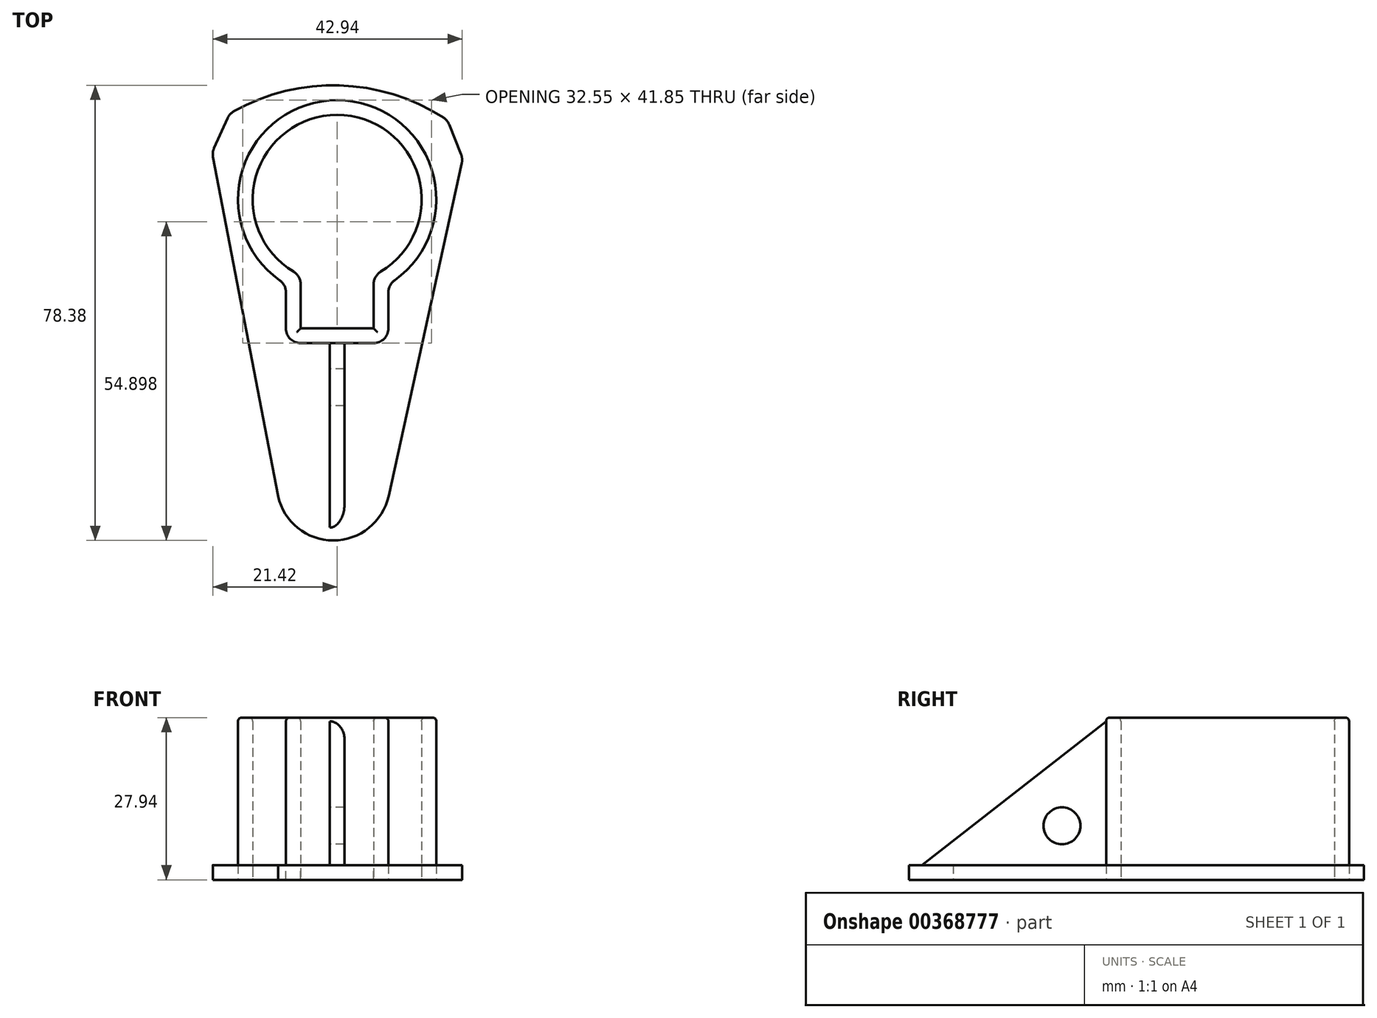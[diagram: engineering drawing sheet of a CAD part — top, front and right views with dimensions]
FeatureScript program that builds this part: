
annotation { "Feature Type Name" : "Feature", "Feature Type Description" : "" }
export const myFeature = defineFeature(function(context is Context, id is Id, definition is map)
    precondition{}
    {
        {
            var Q0;
            Q0=qCreatedBy(makeId("Top.planeOp"),FACE);
            var sketch = newSketch(context, id + "F0", { "sketchPlane" : qUnion([Q0])});
            skCircle(sketch, "E0", {"center": v(0, 0) * mm, "radius": 14.54 * mm, "construction": true});
            skCircle(sketch, "E1", {"center": v(0, 0) * mm, "radius": 17.08 * mm, "construction": true});
            skLineSegment(sketch, "E2.bottom", {"start": v(-6.29, -13.11) * mm, "end": v(6.29, -13.11) * mm, "construction": true});
            skLineSegment(sketch, "E2.top", {"start": v(-6.29, -22.23) * mm, "end": v(6.29, -22.23) * mm, "construction": true});
            skLineSegment(sketch, "E2.left", {"start": v(-6.29, -13.11) * mm, "end": v(-6.29, -22.23) * mm, "construction": true});
            skLineSegment(sketch, "E2.right", {"start": v(6.29, -13.11) * mm, "end": v(6.29, -22.23) * mm, "construction": true});
            skLineSegment(sketch, "E3.bottom", {"start": v(-8.83, -24.77) * mm, "end": v(8.83, -24.77) * mm, "construction": true});
            skLineSegment(sketch, "E3.top", {"start": v(-8.83, -11.56) * mm, "end": v(8.83, -11.56) * mm, "construction": true});
            skLineSegment(sketch, "E3.left", {"start": v(-8.83, -24.77) * mm, "end": v(-8.83, -11.56) * mm, "construction": true});
            skLineSegment(sketch, "E3.right", {"start": v(8.83, -24.77) * mm, "end": v(8.83, -11.56) * mm, "construction": true});
            skArc(sketch, "E4", {"start": v(6.29, -13.11) * mm, "mid": v(0, 14.54) * mm, "end": v(-6.29, -13.11) * mm});
            skArc(sketch, "E5", {"start": v(8.83, -14.62) * mm, "mid": v(0, 17.08) * mm, "end": v(-8.83, -14.62) * mm});
            skLineSegment(sketch, "E6", {"start": v(-6.29, -13.11) * mm, "end": v(-6.29, -22.23) * mm});
            skLineSegment(sketch, "E7", {"start": v(-6.29, -22.23) * mm, "end": v(6.29, -22.23) * mm});
            skLineSegment(sketch, "E8", {"start": v(6.29, -22.23) * mm, "end": v(6.29, -13.11) * mm});
            skLineSegment(sketch, "E9", {"start": v(8.83, -14.62) * mm, "end": v(8.83, -24.77) * mm});
            skLineSegment(sketch, "E10", {"start": v(-8.83, -24.77) * mm, "end": v(-8.83, -14.62) * mm});
            skLineSegment(sketch, "E11", {"start": v(-22.31, 12.18) * mm, "end": v(-10.19, -51.09) * mm});
            skLineSegment(sketch, "E12", {"start": v(-10.19, -51.09) * mm, "end": v(8.86, -51.09) * mm, "construction": true});
            skLineSegment(sketch, "E13", {"start": v(8.86, -51.09) * mm, "end": v(22.5, 10.93) * mm});
            skArc(sketch, "E14", {"start": v(22.5, 10.93) * mm, "mid": v(0.31, 19.62) * mm, "end": v(-22.31, 12.18) * mm});
            skArc(sketch, "E15", {"start": v(-10.19, -51.09) * mm, "mid": v(-0.66, -58.74) * mm, "end": v(8.86, -51.09) * mm});
            skLineSegment(sketch, "E16", {"start": v(-8.83, -24.77) * mm, "end": v(8.83, -24.77) * mm});
            skSolve(sketch);
        }
        {
            var Q0;
            Q0=makeQuery(id+"F0.imprint","IMPRINT",FACE,{"disambiguationData":[TD([[makeQuery(id+"F0.imprint","IMPRINT",EDGE,{"derivedFrom":sQuery(id+"F0.wireOp",EDGE,"E4")}),1.0]])]});
            var Q1;
            Q1=makeQuery(id+"F0.imprint","IMPRINT",FACE,{"disambiguationData":[TD([[makeQuery(id+"F0.imprint","IMPRINT",EDGE,{"derivedFrom":sQuery(id+"F0.wireOp",EDGE,"E5")}),-1.0]])]});
            extrude(context, id + "F1", {"entities" : qUnion([Q0, Q1]), "depth" : 2.54 * mm});
        }
        {
            var Q0;
            Q0=makeQuery(id+"F0.imprint","IMPRINT",FACE,{"disambiguationData":[TD([[makeQuery(id+"F0.imprint","IMPRINT",EDGE,{"derivedFrom":sQuery(id+"F0.wireOp",EDGE,"E4")}),-1.0]])]});
            extrude(context, id + "F2", {"entities" : qUnion([Q0]), "depth" : 27.94 * mm});
        }
        {
            var Q0;
            Q0=makeQuery(id+"F1.opExtrude","SWEPT_EDGE",EDGE,{"disambiguationData":[OSD([sQuery(id+"F0.wireOp",EDGE,"E11"),sQuery(id+"F0.wireOp",EDGE,"E14")])]});
            var Q1;
            Q1=makeQuery(id+"F1.opExtrude","SWEPT_EDGE",EDGE,{"disambiguationData":[OSD([sQuery(id+"F0.wireOp",EDGE,"E13"),sQuery(id+"F0.wireOp",EDGE,"E14")])]});
            chamfer(context, id + "F3", {"entities" : qUnion([Q0, Q1]), "width" : 6.35 * mm, "tangentPropagation" : true});
        }
        {
            var Q0;
            Q0=makeQuery(id+"F2.opExtrude","SWEPT_EDGE",EDGE,{"disambiguationData":[OSD([sQuery(id+"F0.wireOp",EDGE,"E4"),sQuery(id+"F0.wireOp",EDGE,"E6")])]});
            var Q1;
            Q1=makeQuery(id+"F2.opExtrude","SWEPT_EDGE",EDGE,{"disambiguationData":[OSD([sQuery(id+"F0.wireOp",EDGE,"E4"),sQuery(id+"F0.wireOp",EDGE,"E8")])]});
            var Q2;
            Q2=makeQuery(id+"F2.opExtrude","SWEPT_EDGE",EDGE,{"disambiguationData":[OSD([sQuery(id+"F0.wireOp",EDGE,"E10"),sQuery(id+"F0.wireOp",EDGE,"E16")])]});
            var Q3;
            Q3=makeQuery(id+"F2.opExtrude","SWEPT_EDGE",EDGE,{"disambiguationData":[OSD([sQuery(id+"F0.wireOp",EDGE,"E5"),sQuery(id+"F0.wireOp",EDGE,"E10")])]});
            var Q4;
            Q4=makeQuery(id+"F2.opExtrude","SWEPT_EDGE",EDGE,{"disambiguationData":[OSD([sQuery(id+"F0.wireOp",EDGE,"E5"),sQuery(id+"F0.wireOp",EDGE,"E9")])]});
            var Q5;
            Q5=makeQuery(id+"F2.opExtrude","SWEPT_EDGE",EDGE,{"disambiguationData":[OSD([sQuery(id+"F0.wireOp",EDGE,"E9"),sQuery(id+"F0.wireOp",EDGE,"E16")])]});
            fillet(context, id + "F4", {"entities" : qUnion([Q0, Q1, Q2, Q3, Q4, Q5]), "radius" : 2.54 * mm, "tangentPropagation" : true, "allowEdgeOverflow" : false});
        }
        {
            var Q0;
            Q0=makeQuery(id+"F2.opExtrude","CAP_EDGE",EDGE,{"disambiguationData":[OSD([sQuery(id+"F0.wireOp",EDGE,"E4")])],"isStart":false});
            var Q1;
            Q1=makeQuery(id+"F2.opExtrude","CAP_EDGE",EDGE,{"disambiguationData":[OSD([sQuery(id+"F0.wireOp",EDGE,"E7")])],"isStart":false});
            var Q2;
            Q2=makeQuery(id+"F2.opExtrude","CAP_EDGE",EDGE,{"disambiguationData":[OSD([sQuery(id+"F0.wireOp",EDGE,"E5")])],"isStart":false});
            fillet(context, id + "F5", {"entities" : qUnion([Q0, Q1, Q2]), "radius" : 0.64 * mm, "tangentPropagation" : true, "allowEdgeOverflow" : false});
        }
        {
            var Q0;
            Q0=makeQuery(id+"F2.opExtrude","SWEPT_FACE",FACE,{"disambiguationData":[OSD([sQuery(id+"F0.wireOp",EDGE,"E16")])]});
            var sketch = newSketch(context, id + "F6", { "sketchPlane" : qUnion([Q0])});
            skLineSegment(sketch, "E17.bottom", {"start": v(-1.27, 27.3) * mm, "end": v(1.27, 27.3) * mm});
            skLineSegment(sketch, "E17.top", {"start": v(-1.27, 2.54) * mm, "end": v(1.27, 2.54) * mm});
            skLineSegment(sketch, "E17.left", {"start": v(-1.27, 27.3) * mm, "end": v(-1.27, 2.54) * mm});
            skLineSegment(sketch, "E17.right", {"start": v(1.27, 27.3) * mm, "end": v(1.27, 2.54) * mm});
            skLineSegment(sketch, "E18", {"start": v(0, 27.3) * mm, "end": v(0, 23.29) * mm, "construction": true});
            skPoint(sketch, "E18.endSnap0", {"position": v(0, 27.3) * mm});
            skSolve(sketch);
        }
        {
            var Q0;
            Q0=makeQuery(id+"F6.imprint","IMPRINT",FACE,{"disambiguationData":[TD([[makeQuery(id+"F6.imprint","IMPRINT",EDGE,{"derivedFrom":sQuery(id+"F6.wireOp",EDGE,"E17.bottom")}),1.0]])]});
            extrude(context, id + "F7", {"entities" : qUnion([Q0]), "depth" : 31.75 * mm});
        }
        {
            var Q0;
            Q0=makeQuery(id+"F7.opExtrude","SWEPT_FACE",FACE,{"disambiguationData":[OSD([sQuery(id+"F6.wireOp",EDGE,"E17.left")])]});
            var sketch = newSketch(context, id + "F8", { "sketchPlane" : qUnion([Q0])});
            skLineSegment(sketch, "E19", {"start": v(24.77, 27.3) * mm, "end": v(56.52, 2.54) * mm});
            skCircle(sketch, "E20", {"center": v(32.37, 9.3) * mm, "radius": 3.18 * mm});
            skSolve(sketch);
        }
        {
            var Q0;
            Q0=makeQuery(id+"F8.imprint","IMPRINT",FACE,{"disambiguationData":[TD([[makeQuery(id+"F8.imprint","IMPRINT",EDGE,{"derivedFrom":sQuery(id+"F8.wireOp",EDGE,"E19")}),1.0]])]});
            var Q1;
            Q1=makeQuery(id+"F8.imprint","IMPRINT",FACE,{"disambiguationData":[TD([[makeQuery(id+"F8.imprint","IMPRINT",EDGE,{"derivedFrom":sQuery(id+"F8.wireOp",EDGE,"E20")}),1.0]])]});
            extrude(context, id + "F9", {"entities" : qUnion([Q0, Q1]), "operationType" : NewBodyOperationType.REMOVE, "oppositeDirection" : true, "depth" : 25.4 * mm});
        }
        {
            var Q0;
            Q0=makeQuery(id+"F1.opExtrude","SWEPT_EDGE",EDGE,{"disambiguationData":[OSD([sQuery(id+"F0.wireOp",EDGE,"E10"),sQuery(id+"F0.wireOp",EDGE,"E16")])]});
            var Q1;
            Q1=makeQuery(id+"F1.opExtrude","SWEPT_EDGE",EDGE,{"disambiguationData":[OSD([sQuery(id+"F0.wireOp",EDGE,"E5"),sQuery(id+"F0.wireOp",EDGE,"E10")])]});
            var Q2;
            Q2=makeQuery(id+"F1.opExtrude","SWEPT_EDGE",EDGE,{"disambiguationData":[OSD([sQuery(id+"F0.wireOp",EDGE,"E4"),sQuery(id+"F0.wireOp",EDGE,"E6")])]});
            var Q3;
            Q3=makeQuery(id+"F1.opExtrude","SWEPT_EDGE",EDGE,{"disambiguationData":[OSD([sQuery(id+"F0.wireOp",EDGE,"E5"),sQuery(id+"F0.wireOp",EDGE,"E9")])]});
            var Q4;
            Q4=makeQuery(id+"F1.opExtrude","SWEPT_EDGE",EDGE,{"disambiguationData":[OSD([sQuery(id+"F0.wireOp",EDGE,"E4"),sQuery(id+"F0.wireOp",EDGE,"E8")])]});
            var Q5;
            Q5=makeQuery(id+"F1.opExtrude","SWEPT_EDGE",EDGE,{"disambiguationData":[OSD([sQuery(id+"F0.wireOp",EDGE,"E9"),sQuery(id+"F0.wireOp",EDGE,"E16")])]});
            var Q6;
            {var subQ0=sQuery(id+"F0.wireOp",EDGE,"E11");Q6=makeQuery(id+"F3.opChamfer","BLEND_EDGE",EDGE,{"blendedFrom":[makeQuery(id+"F1.opExtrude","SWEPT_EDGE",EDGE,{"disambiguationData":[OSD([subQ0,sQuery(id+"F0.wireOp",EDGE,"E14")])]}),makeQuery(id+"F1.opExtrude","SWEPT_FACE",FACE,{"disambiguationData":[OSD([subQ0])]})],"blendedInto":[makeQuery(id+"F1.opExtrude","SWEPT_FACE",FACE,{"disambiguationData":[OSD([subQ0])]})]});}
            var Q7;
            {var subQ0=sQuery(id+"F0.wireOp",EDGE,"E14");Q7=makeQuery(id+"F3.opChamfer","BLEND_EDGE",EDGE,{"blendedFrom":[makeQuery(id+"F1.opExtrude","SWEPT_EDGE",EDGE,{"disambiguationData":[OSD([sQuery(id+"F0.wireOp",EDGE,"E11"),subQ0])]}),makeQuery(id+"F1.opExtrude","SWEPT_FACE",FACE,{"disambiguationData":[OSD([subQ0])]})],"blendedInto":[makeQuery(id+"F1.opExtrude","SWEPT_FACE",FACE,{"disambiguationData":[OSD([subQ0])]})]});}
            var Q8;
            {var subQ0=sQuery(id+"F0.wireOp",EDGE,"E14");Q8=makeQuery(id+"F3.opChamfer","BLEND_EDGE",EDGE,{"blendedFrom":[makeQuery(id+"F1.opExtrude","SWEPT_EDGE",EDGE,{"disambiguationData":[OSD([sQuery(id+"F0.wireOp",EDGE,"E13"),subQ0])]}),makeQuery(id+"F1.opExtrude","SWEPT_FACE",FACE,{"disambiguationData":[OSD([subQ0])]})],"blendedInto":[makeQuery(id+"F1.opExtrude","SWEPT_FACE",FACE,{"disambiguationData":[OSD([subQ0])]})]});}
            var Q9;
            {var subQ0=sQuery(id+"F0.wireOp",EDGE,"E13");Q9=makeQuery(id+"F3.opChamfer","BLEND_EDGE",EDGE,{"blendedFrom":[makeQuery(id+"F1.opExtrude","SWEPT_EDGE",EDGE,{"disambiguationData":[OSD([subQ0,sQuery(id+"F0.wireOp",EDGE,"E14")])]}),makeQuery(id+"F1.opExtrude","SWEPT_FACE",FACE,{"disambiguationData":[OSD([subQ0])]})],"blendedInto":[makeQuery(id+"F1.opExtrude","SWEPT_FACE",FACE,{"disambiguationData":[OSD([subQ0])]})]});}
            var Q10;
            Q10=makeQuery(id+"F9.boolean.opBoolean","COPY",EDGE,{"derivedFrom":makeQuery(id+"F9.opExtrude","CAP_EDGE",EDGE,{"disambiguationData":[OSD([sQuery(id+"F8.wireOp",EDGE,"E19")])],"isStart":true})});
            var Q11;
            Q11=makeQuery(id+"F9.boolean.opBoolean","INTERSECT",EDGE,{"derivedFrom":[makeQuery(id+"F7.opExtrude","SWEPT_FACE",FACE,{"disambiguationData":[OSD([sQuery(id+"F6.wireOp",EDGE,"E17.right")])]}),makeQuery(id+"F9.opExtrude","SWEPT_FACE",FACE,{"disambiguationData":[OSD([sQuery(id+"F8.wireOp",EDGE,"E19")])]})]});
            fillet(context, id + "F10", {"entities" : qUnion([Q0, Q1, Q2, Q3, Q4, Q5, Q6, Q7, Q8, Q9, Q10, Q11]), "radius" : 2.54 * mm, "tangentPropagation" : true, "allowEdgeOverflow" : false});
        }
    });
